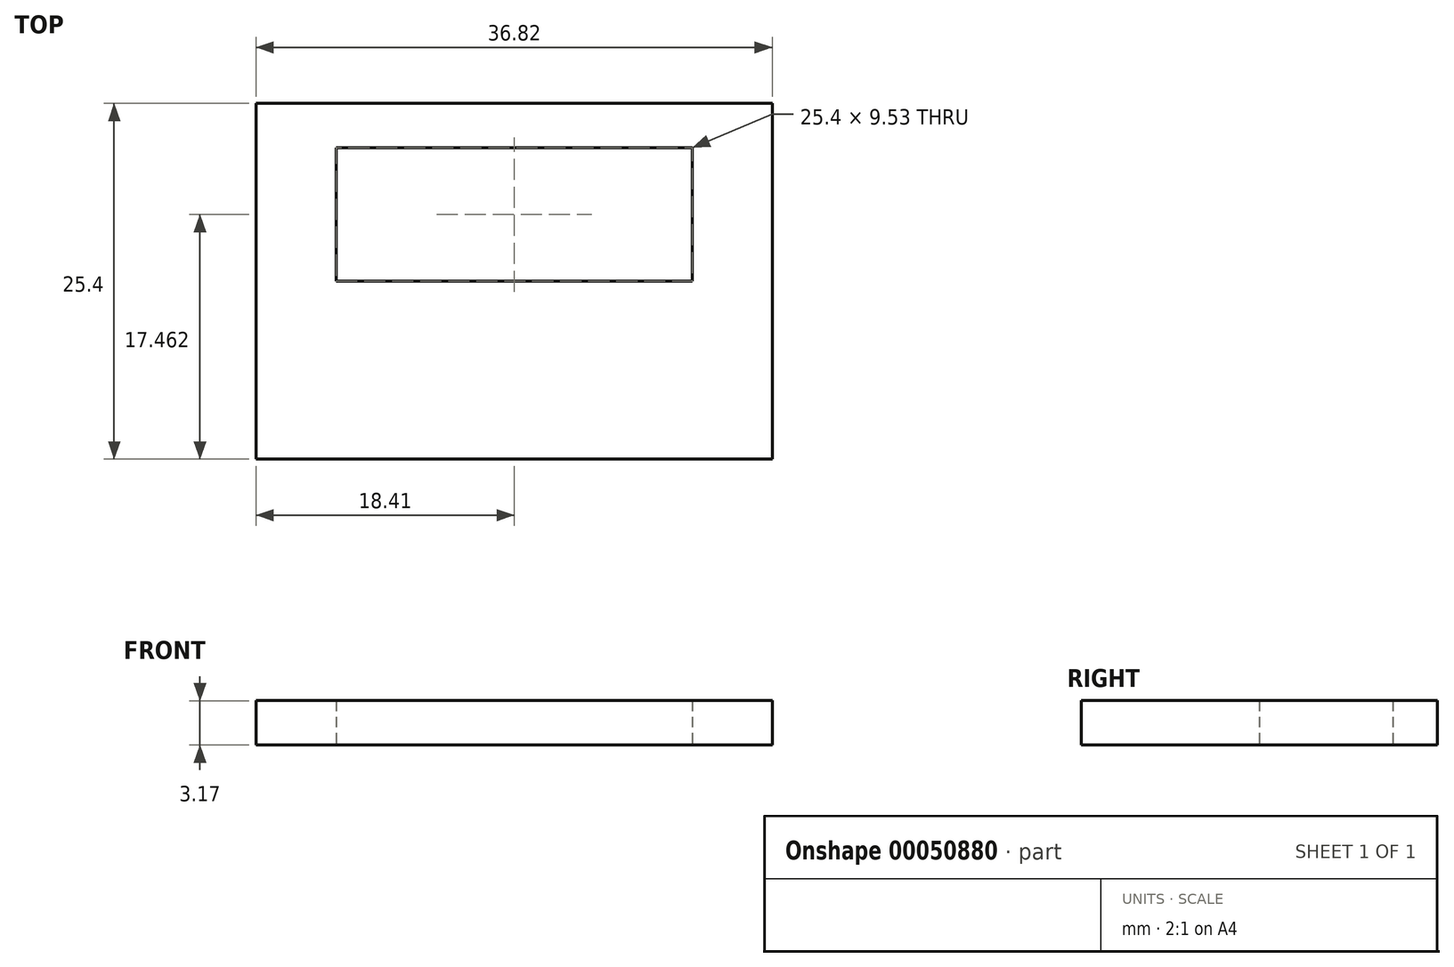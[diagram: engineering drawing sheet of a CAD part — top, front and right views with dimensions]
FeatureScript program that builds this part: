
annotation { "Feature Type Name" : "Feature", "Feature Type Description" : "" }
export const myFeature = defineFeature(function(context is Context, id is Id, definition is map)
    precondition{}
    {
        {
            var Q0;
            Q0=qCreatedBy(makeId("Top.planeOp"),FACE);
            var sketch = newSketch(context, id + "F0", { "sketchPlane" : qUnion([Q0])});
            skLineSegment(sketch, "E0.rect.bottom", {"start": v(-18.41, 12.7) * mm, "end": v(18.41, 12.7) * mm});
            skLineSegment(sketch, "E0.rect.top", {"start": v(-18.41, -12.7) * mm, "end": v(18.41, -12.7) * mm});
            skLineSegment(sketch, "E0.rect.left", {"start": v(-18.41, 12.7) * mm, "end": v(-18.41, -12.7) * mm});
            skLineSegment(sketch, "E0.rect.right", {"start": v(18.42, 12.7) * mm, "end": v(18.41, -12.7) * mm});
            skPoint(sketch, "E0.rect.middle", {"position": v(0, 0) * mm});
            skLineSegment(sketch, "E1.bottom", {"start": v(12.7, 0) * mm, "end": v(-12.7, 0) * mm});
            skLineSegment(sketch, "E1.top", {"start": v(12.7, 9.53) * mm, "end": v(-12.7, 9.53) * mm});
            skLineSegment(sketch, "E1.left", {"start": v(12.7, 0) * mm, "end": v(12.7, 9.53) * mm});
            skLineSegment(sketch, "E1.right", {"start": v(-12.7, 0) * mm, "end": v(-12.7, 9.53) * mm});
            skSolve(sketch);
        }
        {
            var Q0;
            Q0=makeQuery(id+"F0.imprint","IMPRINT",FACE,{"disambiguationData":[TD([[makeQuery(id+"F0.imprint","IMPRINT",EDGE,{"derivedFrom":sQuery(id+"F0.wireOp",EDGE,"E0.rect.bottom")}),-1.0]])]});
            extrude(context, id + "F1", {"entities" : qUnion([Q0]), "depth" : 3.17 * mm});
        }
    });
